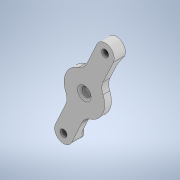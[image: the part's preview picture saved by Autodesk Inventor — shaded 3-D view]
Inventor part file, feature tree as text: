
AUTODESK INVENTOR PART (.ipt)
format: ipt  version: 2020 (Build 240168000, 168)  size: 203,264 bytes
history: native  units: mm
features: reference x5, extrude x4, sketch x4, other x4, fillet x2, chamfer x2, plane x1, projected_geometry x1
ambient origin geometry x8: Origin, YZ Plane, XZ Plane, XY Plane, X Axis, Y Axis, Z Axis, Center Point
bodies: Solid1 (feature_tree)
feature tree (23):
  extrude  "Extrusion1"  Depth=8.0mm
  fillet  "Fillet1"  Radius=3.0mm
  extrude  "Extrusion2"  Depth=4.0mm
  extrude  "Extrusion3"  Depth=12.0mm
  chamfer  "Chamfer1"  Distance=4.0mm
  sketch  "Sketch4"  dims[d9=11.0mm d10=4.0mm d11=1.0mm d12=0.0mm d13=1.0mm d14=2.0mm d15=45.0deg d16=8.0mm d17=8.0mm d18=1.0mm d19=0.0mm d20=2.0mm d21=1.0mm d22=2.0mm d23=45.0deg]
  plane  "Work Plane1"
  extrude  "Extrusion4"  Depth=1.0mm TaperAngle=0.0deg
  fillet  "Fillet2"  Radius=1.0mm
  chamfer  "Chamfer2"  Distance=8.0mm
  sketch  "Sketch1"  dims[d0=18.0mm d1=8.0mm d2=3.0mm d3=0.0mm]
  reference  "Reference1"
  reference  "Reference2"
  reference  "Reference3"
  sketch  "Sketch2"  dims[d4=6.0mm d5=4.0mm]
  reference  "Reference4"
  sketch  "Sketch3"  dims[d6=3.0mm d7=0.0mm d8=12.0mm]
  reference  "Reference5"
  projected_geometry  "Projected Loop1"
  parser-record x1  (decoder bookkeeping rows leaked as tree rows — omitted from the tree; the rows remain in map.json)
  other  "reducer_2.iam"
  other  "bearing_shell_2:1"
  other  "bearing_6_13_5:1"
note: 1 file-system path scrubbed to <path> (originals preserved in map.json)
